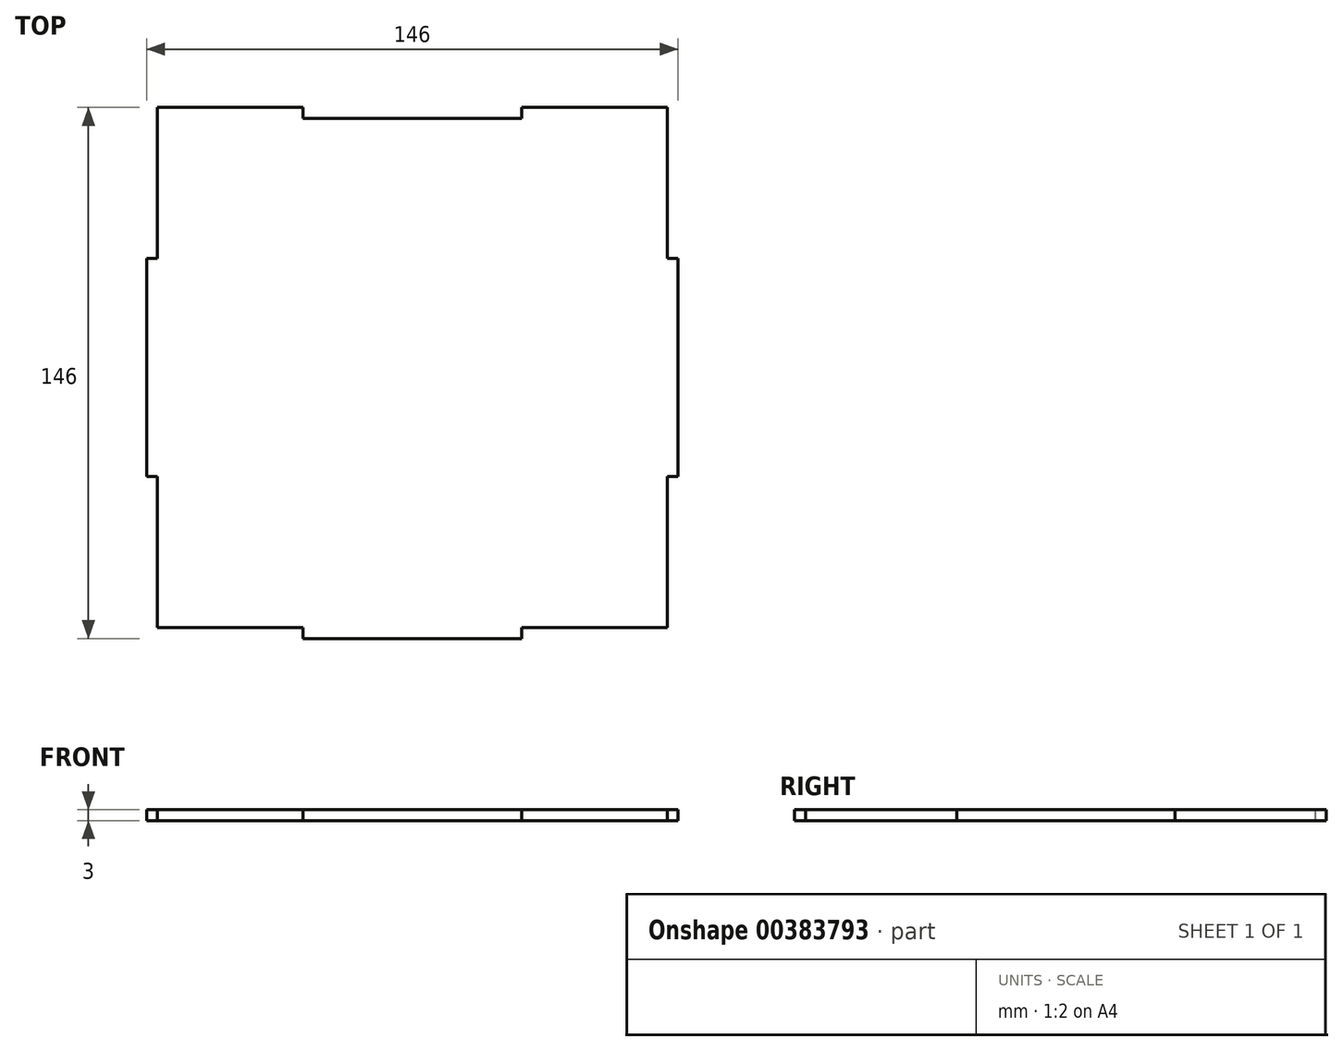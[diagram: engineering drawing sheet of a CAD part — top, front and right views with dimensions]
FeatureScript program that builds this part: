
annotation { "Feature Type Name" : "Feature", "Feature Type Description" : "" }
export const myFeature = defineFeature(function(context is Context, id is Id, definition is map)
    precondition{}
    {
        {
            var Q0;
            Q0=qCreatedBy(makeId("Top.planeOp"),FACE);
            var sketch = newSketch(context, id + "F0", { "sketchPlane" : qUnion([Q0])});
            skLineSegment(sketch, "E0.bottom", {"start": v(70, -71.5) * mm, "end": v(30, -71.5) * mm});
            skLineSegment(sketch, "E0.top", {"start": v(70, 71.5) * mm, "end": v(30, 71.5) * mm});
            skLineSegment(sketch, "E0.left", {"start": v(70, -71.5) * mm, "end": v(70, -30) * mm});
            skLineSegment(sketch, "E0.right", {"start": v(-70, -71.5) * mm, "end": v(-70, -30) * mm});
            skPoint(sketch, "E0.middle", {"position": v(0, 0) * mm});
            skLineSegment(sketch, "E1.bottom", {"start": v(30, -74.5) * mm, "end": v(-30, -74.5) * mm});
            skLineSegment(sketch, "E1.left", {"start": v(30, -74.5) * mm, "end": v(30, -71.5) * mm});
            skLineSegment(sketch, "E1.right", {"start": v(-30, -74.5) * mm, "end": v(-30, -71.5) * mm});
            skPoint(sketch, "E1.middle", {"position": v(0, -71.5) * mm});
            skPoint(sketch, "E2.orphan", {"position": v(-30, -68.5) * mm});
            skPoint(sketch, "E3.orphan", {"position": v(30, -68.5) * mm});
            skLineSegment(sketch, "E4.trimOffspring", {"start": v(-30, -71.5) * mm, "end": v(-70, -71.5) * mm});
            skLineSegment(sketch, "E5.bottom", {"start": v(30, 68.5) * mm, "end": v(-30, 68.5) * mm});
            skLineSegment(sketch, "E5.left", {"start": v(30, 68.5) * mm, "end": v(30, 71.5) * mm});
            skLineSegment(sketch, "E5.right", {"start": v(-30, 68.5) * mm, "end": v(-30, 71.5) * mm});
            skPoint(sketch, "E5.middle", {"position": v(0, 71.5) * mm});
            skPoint(sketch, "E6.orphan", {"position": v(-30, 74.5) * mm});
            skLineSegment(sketch, "E7.trimOffspring", {"start": v(-30, 71.5) * mm, "end": v(-70, 71.5) * mm});
            skPoint(sketch, "E8.orphan", {"position": v(30, 74.5) * mm});
            skLineSegment(sketch, "E9.bottom", {"start": v(-70, -30) * mm, "end": v(-73, -30) * mm});
            skLineSegment(sketch, "E9.top", {"start": v(-70, 30) * mm, "end": v(-73, 30) * mm});
            skLineSegment(sketch, "E9.right", {"start": v(-73, -30) * mm, "end": v(-73, 30) * mm});
            skPoint(sketch, "E9.middle", {"position": v(-70, 0) * mm});
            skLineSegment(sketch, "E10.trimOffspring", {"start": v(-70, 30) * mm, "end": v(-70, 71.5) * mm});
            skPoint(sketch, "E9.left.end.orphan", {"position": v(-67, 30) * mm});
            skPoint(sketch, "E9.left.start.orphan", {"position": v(-67, -30) * mm});
            skLineSegment(sketch, "E11.bottom", {"start": v(73, -30) * mm, "end": v(70, -30) * mm});
            skLineSegment(sketch, "E11.top", {"start": v(73, 30) * mm, "end": v(70, 30) * mm});
            skLineSegment(sketch, "E11.left", {"start": v(73, -30) * mm, "end": v(73, 30) * mm});
            skPoint(sketch, "E11.middle", {"position": v(70, 0) * mm});
            skPoint(sketch, "E11.right.end.orphan", {"position": v(67, 30) * mm});
            skPoint(sketch, "E11.right.start.orphan", {"position": v(67, -30) * mm});
            skLineSegment(sketch, "E12.trimOffspring", {"start": v(70, 30) * mm, "end": v(70, 71.5) * mm});
            skSolve(sketch);
        }
        {
            var Q0;
            Q0 = qSketchRegion(id + "F0", true);
            extrude(context, id + "F1", {"entities" : qUnion([Q0]), "depth" : 3 * mm});
        }
    });
